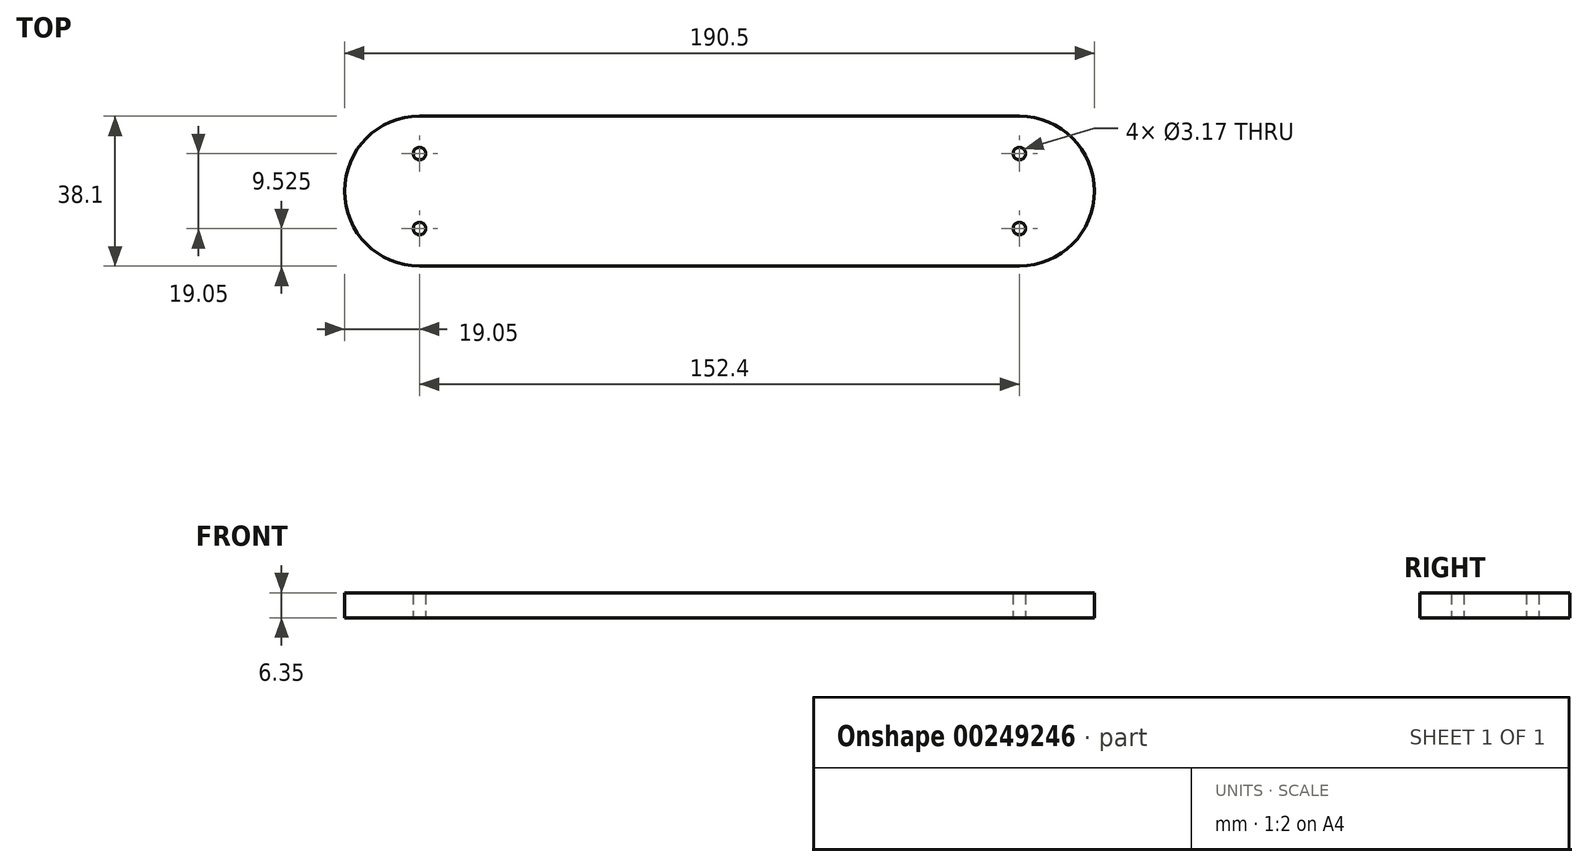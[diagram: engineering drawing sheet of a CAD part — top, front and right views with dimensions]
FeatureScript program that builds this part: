
annotation { "Feature Type Name" : "Feature", "Feature Type Description" : "" }
export const myFeature = defineFeature(function(context is Context, id is Id, definition is map)
    precondition{}
    {
        {
            var Q0;
            Q0=qCreatedBy(makeId("Top.planeOp"),FACE);
            var sketch = newSketch(context, id + "F0", { "sketchPlane" : qUnion([Q0])});
            skLineSegment(sketch, "E0", {"start": v(0, 0) * mm, "end": v(152.4, 0) * mm});
            skArc(sketch, "E1", {"start": v(0, 0) * mm, "mid": v(-19.05, -19.05) * mm, "end": v(0, -38.1) * mm});
            skLineSegment(sketch, "E2", {"start": v(0, -38.1) * mm, "end": v(152.4, -38.1) * mm});
            skArc(sketch, "E3", {"start": v(152.4, -38.1) * mm, "mid": v(171.45, -19.05) * mm, "end": v(152.4, 0) * mm});
            skCircle(sketch, "E4", {"center": v(0, -28.58) * mm, "radius": 1.59 * mm});
            skCircle(sketch, "E5", {"center": v(0, -9.52) * mm, "radius": 1.59 * mm});
            skCircle(sketch, "E6", {"center": v(152.4, -9.52) * mm, "radius": 1.59 * mm});
            skCircle(sketch, "E7", {"center": v(152.4, -28.57) * mm, "radius": 1.59 * mm});
            skSolve(sketch);
        }
        {
            var Q0;
            Q0=makeQuery(id+"F0.imprint","IMPRINT",FACE,{"disambiguationData":[TD([[makeQuery(id+"F0.imprint","IMPRINT",EDGE,{"derivedFrom":sQuery(id+"F0.wireOp",EDGE,"E0")}),-1.0]])]});
            extrude(context, id + "F1", {"entities" : qUnion([Q0]), "depth" : 6.35 * mm});
        }
    });
